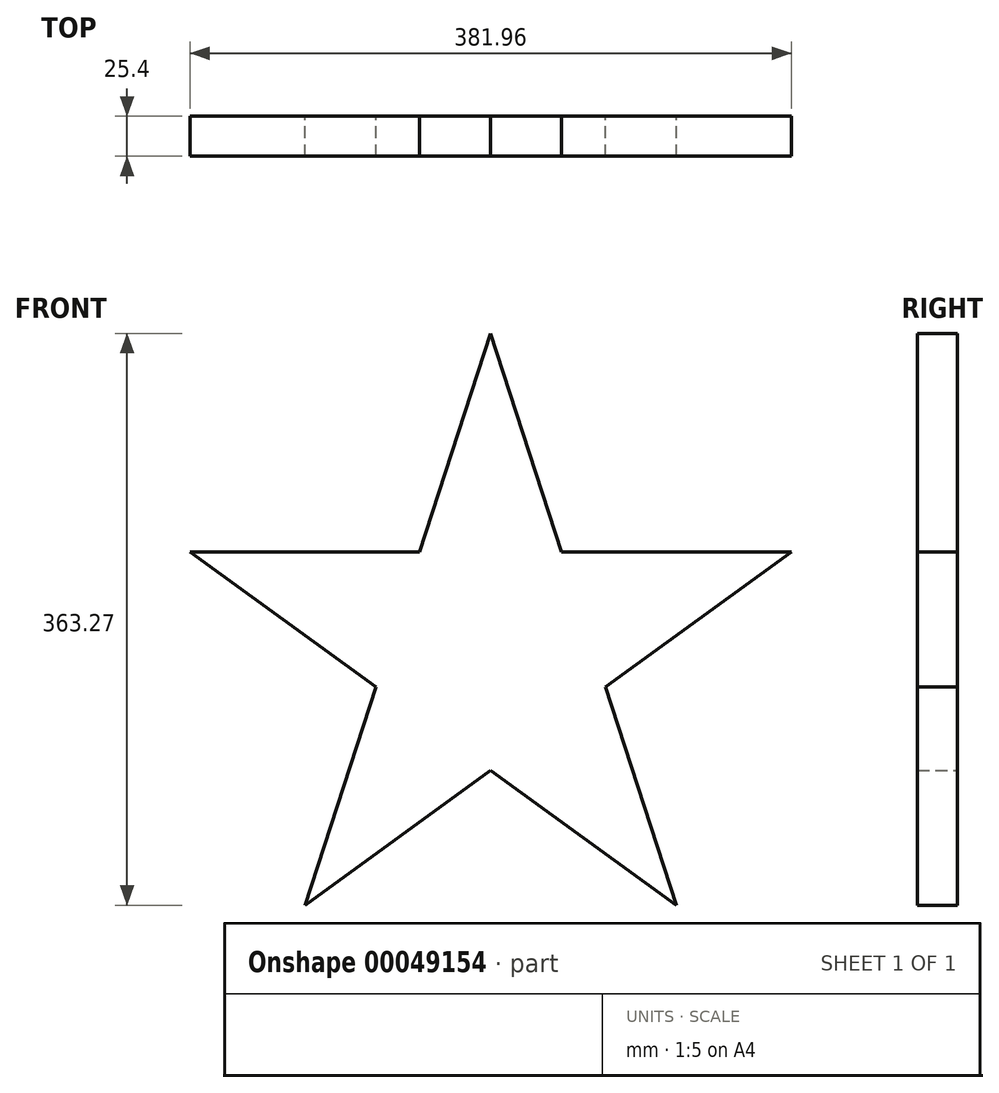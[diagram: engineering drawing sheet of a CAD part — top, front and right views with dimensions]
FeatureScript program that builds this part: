
annotation { "Feature Type Name" : "Feature", "Feature Type Description" : "" }
export const myFeature = defineFeature(function(context is Context, id is Id, definition is map)
    precondition{}
    {
        {
            var Q0;
            Q0=qCreatedBy(makeId("Front.planeOp"),FACE);
            var sketch = newSketch(context, id + "F0", { "sketchPlane" : qUnion([Q0])});
            skLineSegment(sketch, "E0", {"start": v(-45.08, 62.05) * mm, "end": v(45.08, 62.05) * mm});
            skLineSegment(sketch, "E1", {"start": v(45.08, 62.05) * mm, "end": v(72.95, -23.7) * mm});
            skLineSegment(sketch, "E2", {"start": v(72.95, -23.7) * mm, "end": v(0, -76.7) * mm});
            skLineSegment(sketch, "E3", {"start": v(0, -76.7) * mm, "end": v(-72.95, -23.7) * mm});
            skLineSegment(sketch, "E4", {"start": v(-72.95, -23.7) * mm, "end": v(-45.08, 62.05) * mm});
            skLineSegment(sketch, "E5", {"start": v(-45.08, 62.05) * mm, "end": v(36.47, -50.2) * mm, "construction": true});
            skLineSegment(sketch, "E6", {"start": v(0, -76.7) * mm, "end": v(0, 62.05) * mm, "construction": true});
            skPoint(sketch, "E7", {"position": v(0, 0) * mm});
            skLineSegment(sketch, "E8", {"start": v(-45.08, 62.05) * mm, "end": v(-190.98, 62.05) * mm, "construction": true});
            skLineSegment(sketch, "E9", {"start": v(-72.95, -23.7) * mm, "end": v(-190.98, 62.05) * mm, "construction": true});
            skLineSegment(sketch, "E10", {"start": v(-190.98, 62.05) * mm, "end": v(-72.95, -23.7) * mm});
            skLineSegment(sketch, "E11", {"start": v(-190.98, 62.05) * mm, "end": v(-45.08, 62.05) * mm});
            skLineSegment(sketch, "E12", {"start": v(-45.08, 62.05) * mm, "end": v(0, 200.81) * mm});
            skLineSegment(sketch, "E13", {"start": v(0, 200.81) * mm, "end": v(45.08, 62.05) * mm});
            skLineSegment(sketch, "E14", {"start": v(45.08, 62.05) * mm, "end": v(190.98, 62.05) * mm});
            skLineSegment(sketch, "E15", {"start": v(190.98, 62.05) * mm, "end": v(72.95, -23.7) * mm});
            skLineSegment(sketch, "E16", {"start": v(72.95, -23.7) * mm, "end": v(118.03, -162.46) * mm});
            skLineSegment(sketch, "E17", {"start": v(118.03, -162.46) * mm, "end": v(0, -76.7) * mm});
            skLineSegment(sketch, "E18", {"start": v(-72.95, -23.7) * mm, "end": v(-118.03, -162.46) * mm});
            skLineSegment(sketch, "E19", {"start": v(-118.03, -162.46) * mm, "end": v(0, -76.7) * mm});
            skLineSegment(sketch, "E20", {"start": v(0, 200.81) * mm, "end": v(0, 0) * mm});
            skLineSegment(sketch, "E21", {"start": v(-118.03, -162.46) * mm, "end": v(0, 0) * mm});
            skLineSegment(sketch, "E22", {"start": v(-190.98, 62.05) * mm, "end": v(0, 0) * mm});
            skLineSegment(sketch, "E23", {"start": v(190.98, 62.05) * mm, "end": v(0, 0) * mm});
            skLineSegment(sketch, "E24", {"start": v(118.03, -162.46) * mm, "end": v(0, 0) * mm});
            skLineSegment(sketch, "E25", {"start": v(0, 0) * mm, "end": v(-72.95, -23.7) * mm});
            skLineSegment(sketch, "E26", {"start": v(0, 0) * mm, "end": v(0, -76.7) * mm});
            skLineSegment(sketch, "E27", {"start": v(0, 0) * mm, "end": v(-45.08, 62.05) * mm});
            skLineSegment(sketch, "E28", {"start": v(0, 0) * mm, "end": v(45.08, 62.05) * mm});
            skLineSegment(sketch, "E29", {"start": v(0, 0) * mm, "end": v(72.95, -23.7) * mm});
            skSolve(sketch);
        }
        {
            var Q0;
            Q0 = qSketchRegion(id + "F0", true);
            extrude(context, id + "F1", {"entities" : qUnion([Q0]), "depth" : 25.4 * mm});
        }
    });
